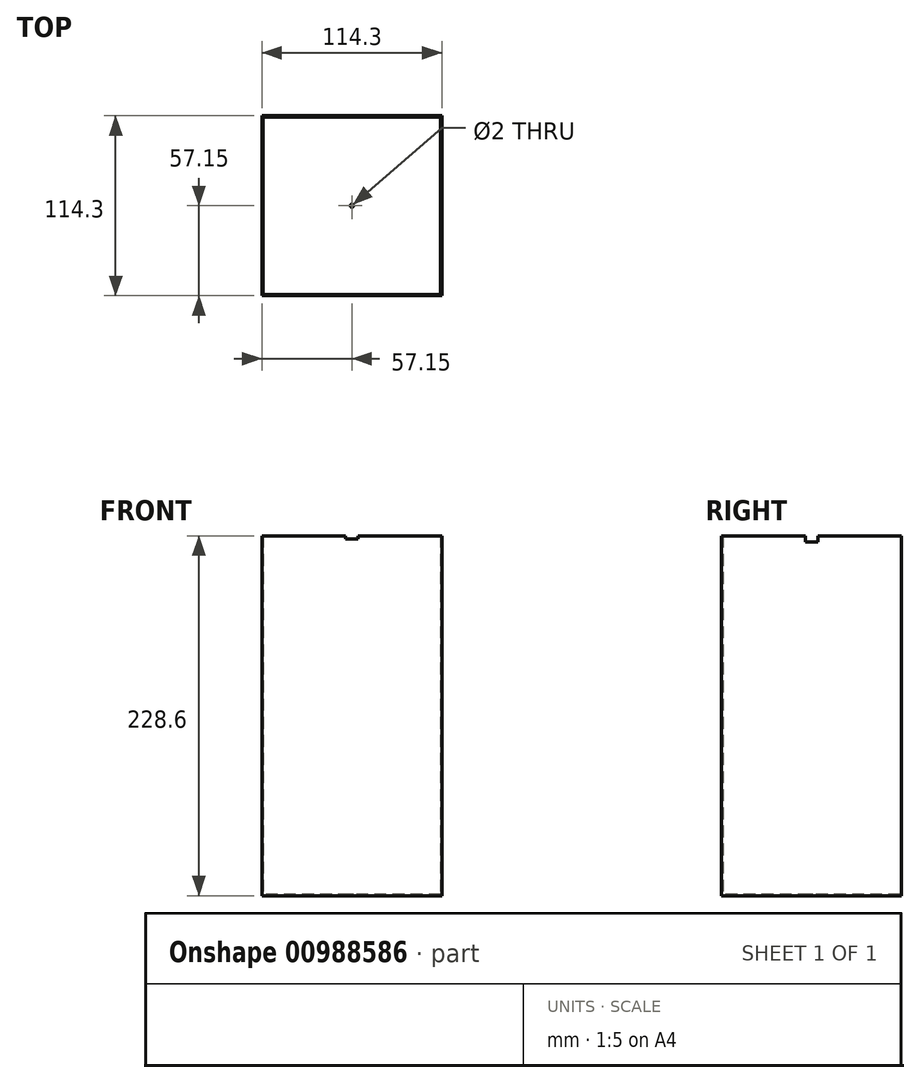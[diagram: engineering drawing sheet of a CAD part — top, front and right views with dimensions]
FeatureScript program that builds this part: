
annotation { "Feature Type Name" : "Feature", "Feature Type Description" : "" }
export const myFeature = defineFeature(function(context is Context, id is Id, definition is map)
    precondition{}
    {
        {
            var Q0;
            Q0=qCreatedBy(makeId("Top.planeOp"),FACE);
            var sketch = newSketch(context, id + "F0", { "sketchPlane" : qUnion([Q0])});
            skLineSegment(sketch, "E0.bottom", {"start": v(57.15, 57.15) * mm, "end": v(-57.15, 57.15) * mm});
            skLineSegment(sketch, "E0.top", {"start": v(57.15, -57.15) * mm, "end": v(-57.15, -57.15) * mm});
            skLineSegment(sketch, "E0.left", {"start": v(57.15, 57.15) * mm, "end": v(57.15, -57.15) * mm});
            skLineSegment(sketch, "E0.right", {"start": v(-57.15, 57.15) * mm, "end": v(-57.15, -57.15) * mm});
            skPoint(sketch, "E0.middle", {"position": v(0, 0) * mm});
            skSolve(sketch);
        }
        {
            var Q0;
            Q0 = qSketchRegion(id + "F0", true);
            extrude(context, id + "F1", {"entities" : qUnion([Q0]), "depth" : 228.6 * mm, "offsetDistance" : 25.4 * mm});
        }
        {
            var Q0;
            Q0=makeQuery(id+"F1.opExtrude","CAP_FACE",FACE,{"disambiguationData":[OSD([sQuery(id+"F0.wireOp",EDGE,"E0.bottom"),sQuery(id+"F0.wireOp",EDGE,"E0.top"),sQuery(id+"F0.wireOp",EDGE,"E0.left"),sQuery(id+"F0.wireOp",EDGE,"E0.right")])],"isStart":false});
            shell(context, id + "F2", {"entities" : qUnion([Q0]), "thickness" : 0.8 * mm});
        }
        {
            var Q0;
            Q0=makeQuery(id+"F2.opShell","OFFSET_FACE",FACE,{"disambiguationData":[OSD([sQuery(id+"F0.wireOp",EDGE,"E0.bottom"),sQuery(id+"F0.wireOp",EDGE,"E0.top"),sQuery(id+"F0.wireOp",EDGE,"E0.left"),sQuery(id+"F0.wireOp",EDGE,"E0.right")])]});
            var sketch = newSketch(context, id + "F3", { "sketchPlane" : qUnion([Q0])});
            skCircle(sketch, "E1", {"center": v(0, 0) * mm, "radius": 1 * mm});
            skSolve(sketch);
        }
        {
            var Q0;
            Q0 = qSketchRegion(id + "F3", true);
            extrude(context, id + "F4", {"entities" : qUnion([Q0]), "operationType" : NewBodyOperationType.REMOVE, "oppositeDirection" : true, "depth" : 25.4 * mm, "offsetDistance" : 25.4 * mm});
        }
        {
            var Q0;
            Q0=makeQuery(id+"F1.opExtrude","SWEPT_FACE",FACE,{"disambiguationData":[OSD([sQuery(id+"F0.wireOp",EDGE,"E0.top")])]});
            var sketch = newSketch(context, id + "F5", { "sketchPlane" : qUnion([Q0])});
            skLineSegment(sketch, "E2", {"start": v(-4, 228.6) * mm, "end": v(4, 228.6) * mm});
            skLineSegment(sketch, "E3", {"start": v(-4, 228.6) * mm, "end": v(-4, 226.6) * mm});
            skLineSegment(sketch, "E4", {"start": v(4, 228.6) * mm, "end": v(4, 226.6) * mm});
            skLineSegment(sketch, "E5", {"start": v(4, 226.6) * mm, "end": v(-4, 226.6) * mm});
            skSolve(sketch);
        }
        {
            var Q0;
            Q0 = qSketchRegion(id + "F5", true);
            extrude(context, id + "F6", {"entities" : qUnion([Q0]), "operationType" : NewBodyOperationType.REMOVE, "endBound" : BoundingType.THROUGH_ALL, "oppositeDirection" : true, "depth" : 25.4 * mm, "offsetDistance" : 25.4 * mm});
        }
        {
            var Q0;
            Q0=makeQuery(id+"F1.opExtrude","SWEPT_FACE",FACE,{"disambiguationData":[OSD([sQuery(id+"F0.wireOp",EDGE,"E0.left")])]});
            var sketch = newSketch(context, id + "F7", { "sketchPlane" : qUnion([Q0])});
            skLineSegment(sketch, "E6", {"start": v(-4, 228.6) * mm, "end": v(4, 228.6) * mm});
            skLineSegment(sketch, "E7", {"start": v(-4, 228.6) * mm, "end": v(-4, 224.6) * mm});
            skLineSegment(sketch, "E8", {"start": v(4, 228.6) * mm, "end": v(4, 224.6) * mm});
            skLineSegment(sketch, "E9", {"start": v(4, 224.6) * mm, "end": v(-4, 224.6) * mm});
            skSolve(sketch);
        }
        {
            var Q0;
            Q0 = qSketchRegion(id + "F7", true);
            extrude(context, id + "F8", {"entities" : qUnion([Q0]), "operationType" : NewBodyOperationType.REMOVE, "endBound" : BoundingType.THROUGH_ALL, "oppositeDirection" : true, "depth" : 25.4 * mm, "offsetDistance" : 25.4 * mm});
        }
    });
